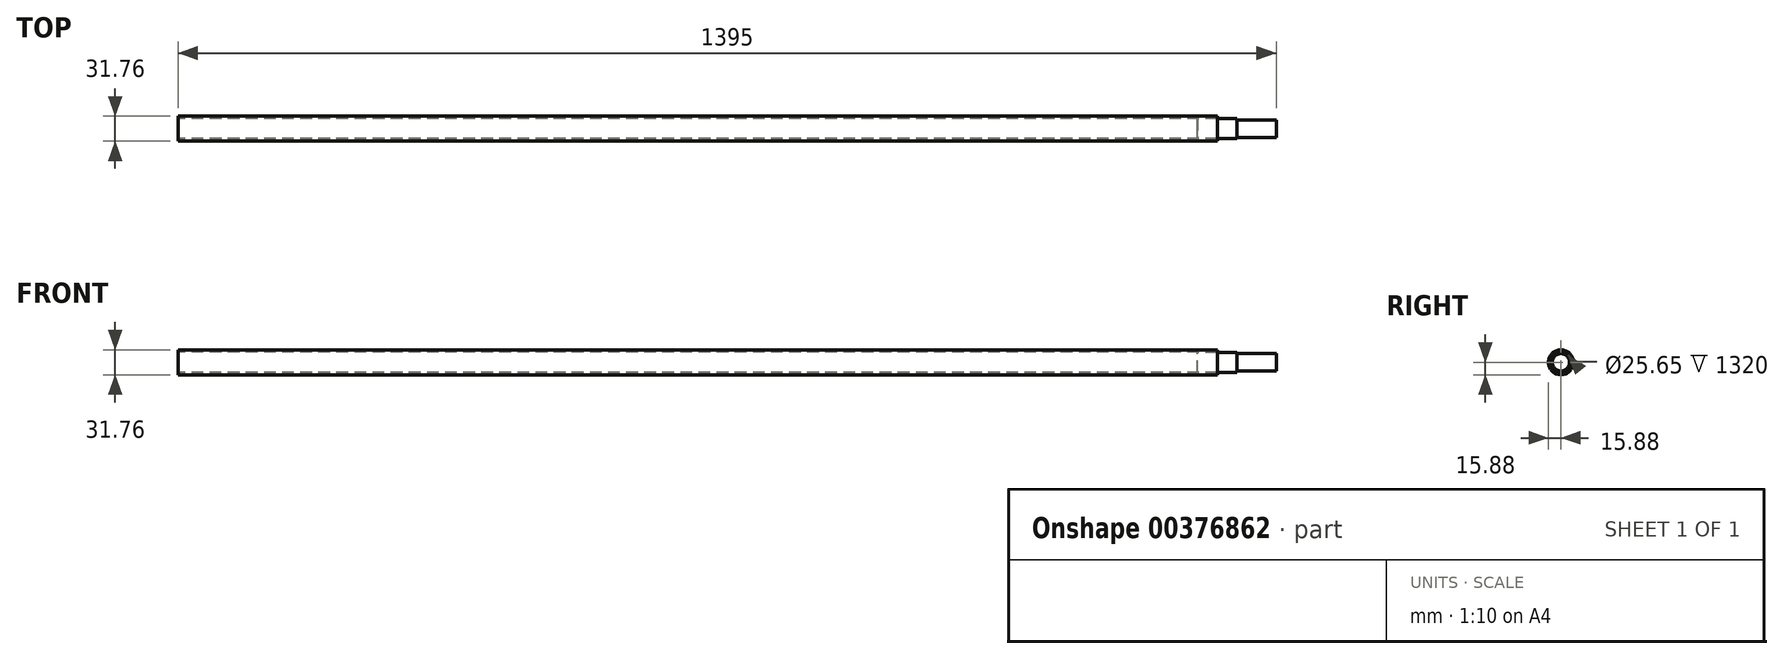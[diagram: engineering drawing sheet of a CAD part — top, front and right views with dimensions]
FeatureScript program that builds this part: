
annotation { "Feature Type Name" : "Feature", "Feature Type Description" : "" }
export const myFeature = defineFeature(function(context is Context, id is Id, definition is map)
    precondition{}
    {
        {
            var Q0;
            Q0=qCreatedBy(makeId("Right.planeOp"),FACE);
            var sketch = newSketch(context, id + "F0", { "sketchPlane" : qUnion([Q0])});
            skCircle(sketch, "E0", {"center": v(0, 0) * mm, "radius": 15.88 * mm});
            skCircle(sketch, "E1", {"center": v(0, 0) * mm, "radius": 12.83 * mm});
            skSolve(sketch);
        }
        {
            var Q0;
            Q0=makeQuery(id+"F0.imprint","IMPRINT",FACE,{"disambiguationData":[TD([[makeQuery(id+"F0.imprint","IMPRINT",EDGE,{"derivedFrom":sQuery(id+"F0.wireOp",EDGE,"E0")}),1.0]])]});
            extrude(context, id + "F1", {"entities" : qUnion([Q0]), "depth" : 1320 * mm, "offsetDistance" : 25 * mm});
        }
        {
            var Q0;
            Q0=makeQuery(id+"F1.opExtrude","CAP_FACE",FACE,{"disambiguationData":[OSD([sQuery(id+"F0.wireOp",EDGE,"E0"),sQuery(id+"F0.wireOp",EDGE,"E1")])],"isStart":false});
            var sketch = newSketch(context, id + "F2", { "sketchPlane" : qUnion([Q0])});
            skCircle(sketch, "E2", {"center": v(0, 0) * mm, "radius": 12.7 * mm});
            skSolve(sketch);
        }
        {
            var Q0;
            Q0=makeQuery(id+"F2.imprint","IMPRINT",FACE,{"disambiguationData":[TD([[makeQuery(id+"F2.imprint","IMPRINT",EDGE,{"derivedFrom":sQuery(id+"F2.wireOp",EDGE,"E2")}),1.0]])]});
            extrude(context, id + "F3", {"entities" : qUnion([Q0]), "depth" : 75 * mm, "offsetDistance" : 25 * mm});
        }
        {
            var Q0;
            Q0=makeQuery(id+"F3.opExtrude","CAP_FACE",FACE,{"disambiguationData":[OSD([sQuery(id+"F2.wireOp",EDGE,"E2")])],"isStart":false});
            var sketch = newSketch(context, id + "F4", { "sketchPlane" : qUnion([Q0])});
            skCircle(sketch, "E3", {"center": v(0, 0) * mm, "radius": 11 * mm});
            skCircle(sketch, "E4", {"center": v(0, 0) * mm, "radius": 35.3 * mm});
            skSolve(sketch);
        }
        {
            var Q0;
            Q0=makeQuery(id+"F4.imprint","IMPRINT",FACE,{"disambiguationData":[TD([[makeQuery(id+"F4.imprint","IMPRINT",EDGE,{"derivedFrom":sQuery(id+"F4.wireOp",EDGE,"E3")}),-1.0]])]});
            extrude(context, id + "F5", {"entities" : qUnion([Q0]), "operationType" : NewBodyOperationType.REMOVE, "oppositeDirection" : true, "depth" : 50 * mm, "offsetDistance" : 25 * mm});
        }
        {
            var Q0;
            Q0=makeQuery(id+"F3.opExtrude","CAP_FACE",FACE,{"disambiguationData":[OSD([sQuery(id+"F2.wireOp",EDGE,"E2")])],"isStart":true});
            var sketch = newSketch(context, id + "F6", { "sketchPlane" : qUnion([Q0])});
            skCircle(sketch, "E5", {"center": v(0, 0) * mm, "radius": 12.7 * mm});
            skSolve(sketch);
        }
        {
            var Q0;
            Q0=makeQuery(id+"F6.imprint","IMPRINT",FACE,{"disambiguationData":[TD([[makeQuery(id+"F6.imprint","IMPRINT",EDGE,{"derivedFrom":sQuery(id+"F6.wireOp",EDGE,"E5")}),-1.0]])]});
            extrude(context, id + "F7", {"entities" : qUnion([Q0]), "operationType" : NewBodyOperationType.ADD, "depth" : 25 * mm, "offsetDistance" : 25 * mm});
        }
    });
